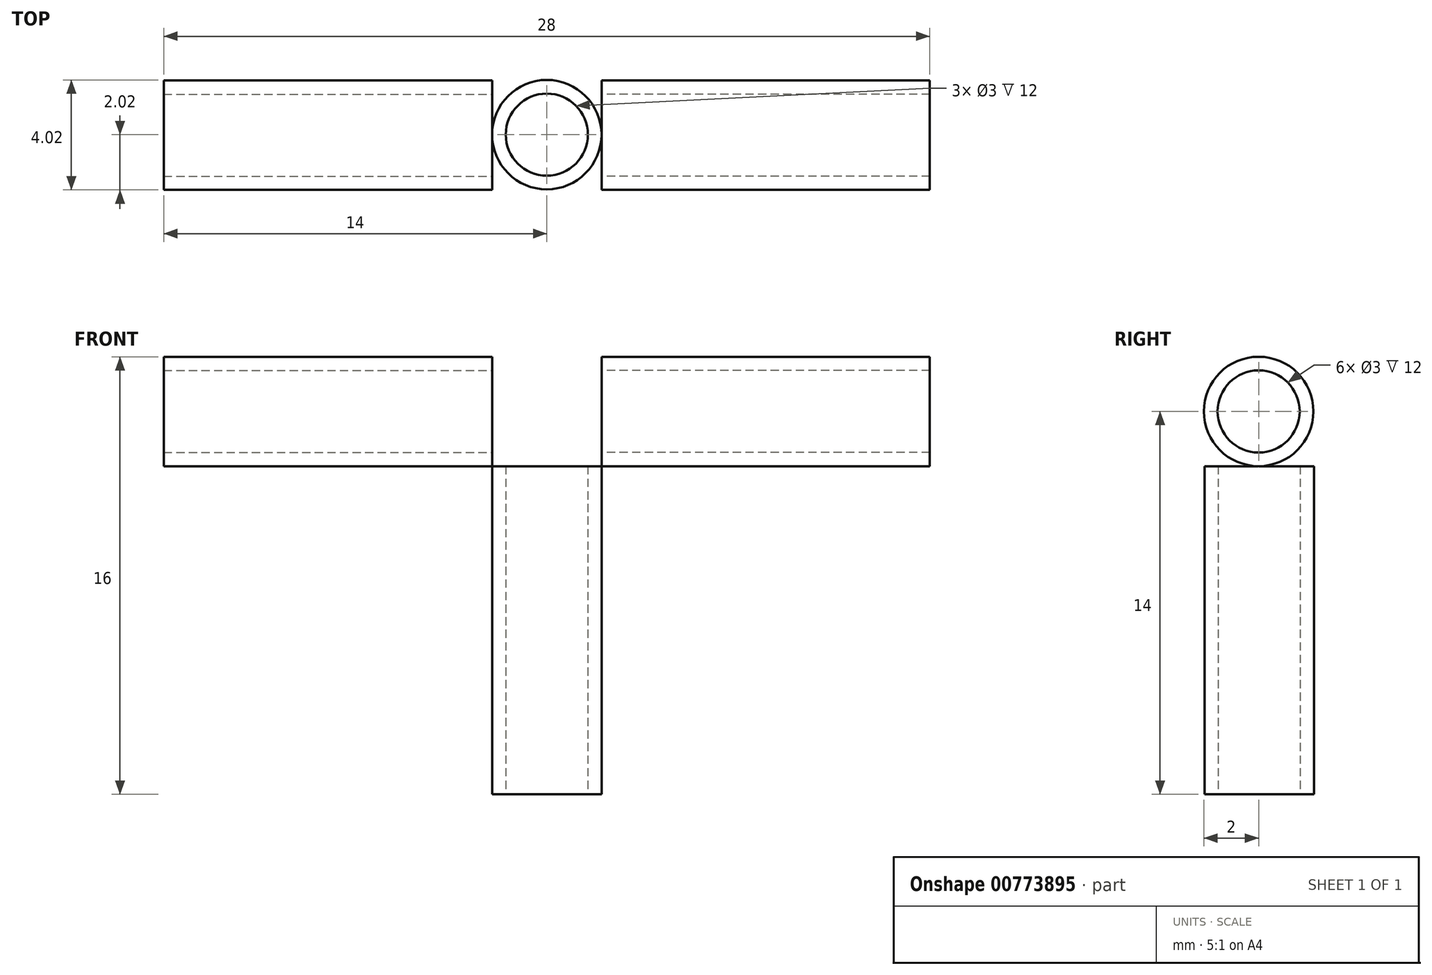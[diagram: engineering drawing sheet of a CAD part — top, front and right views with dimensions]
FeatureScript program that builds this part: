
annotation { "Feature Type Name" : "Feature", "Feature Type Description" : "" }
export const myFeature = defineFeature(function(context is Context, id is Id, definition is map)
    precondition{}
    {
        {
            var Q0;
            Q0=qCreatedBy(makeId("Top.planeOp"),FACE);
            var sketch = newSketch(context, id + "F0", { "sketchPlane" : qUnion([Q0])});
            skCircle(sketch, "E0", {"center": v(0, 0) * mm, "radius": 2 * mm});
            skCircle(sketch, "E1", {"center": v(0, 0) * mm, "radius": 1.5 * mm});
            skSolve(sketch);
        }
        {
            var Q0;
            Q0 = qSketchRegion(id + "F0", true);
            extrude(context, id + "F1", {"entities" : qUnion([Q0]), "depth" : 12 * mm, "offsetDistance" : 25.4 * mm});
        }
        {
            var Q0;
            Q0=qCreatedBy(makeId("Right.planeOp"),FACE);
            var sketch = newSketch(context, id + "F2", { "sketchPlane" : qUnion([Q0])});
            skPoint(sketch, "E2", {"position": v(0, 12) * mm});
            skCircle(sketch, "E3", {"center": v(-0.02, 14) * mm, "radius": 2 * mm});
            skPoint(sketch, "E3.second.point", {"position": v(0, 16) * mm});
            skPoint(sketch, "E3.third.point", {"position": v(1.95, 13.68) * mm});
            skCircle(sketch, "E4", {"center": v(-0.02, 14) * mm, "radius": 1.5 * mm});
            skSolve(sketch);
        }
        {
            var Q0;
            Q0 = qSketchRegion(id + "F2", true);
            extrude(context, id + "F3", {"entities" : qUnion([Q0]), "depth" : 14 * mm, "offsetDistance" : 25.4 * mm, "hasSecondDirection" : true, "secondDirectionOppositeDirection" : false, "secondDirectionDepth" : 2 * mm});
        }
        {
            var Q0;
            Q0 = qSketchRegion(id + "F2", true);
            extrude(context, id + "F4", {"entities" : qUnion([Q0]), "oppositeDirection" : true, "depth" : 14 * mm, "offsetDistance" : 25.4 * mm, "hasSecondDirection" : true, "secondDirectionOppositeDirection" : true, "secondDirectionDepth" : 2 * mm});
        }
    });
